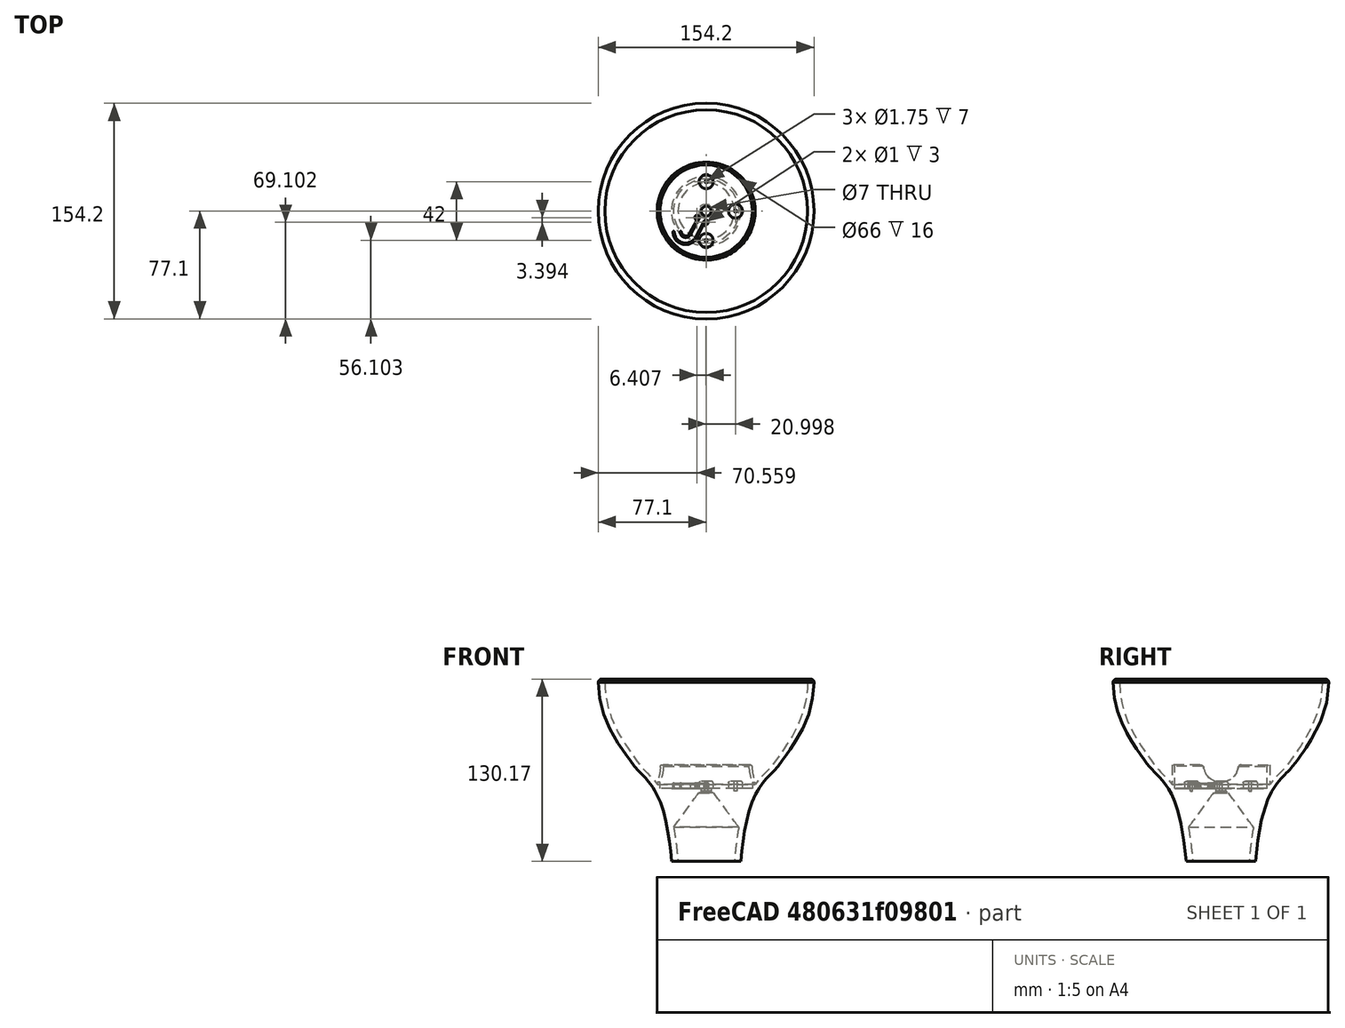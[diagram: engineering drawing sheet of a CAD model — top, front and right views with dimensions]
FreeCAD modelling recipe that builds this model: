
FCSTD DOCUMENT  (FreeCAD 0.21R33771 (Git))
Label: lampshade post-merge
License: All rights reserved
LicenseURL: http://en.wikipedia.org/wiki/All_rights_reserved
objects: Sketcher::SketchObject×10, PartDesign::Pocket×5, PartDesign::Fillet×4, PartDesign::Pad×3, PartDesign::Body×3, PartDesign::Chamfer×2, Part::Feature×2, Mesh::Feature×1, Part::Refine×1, PartDesign::Revolution×1, Part::FeaturePython×1, PartDesign::FeatureBase×1, PartDesign::PolarPattern×1, App::Part×1
note: 49 computed .brp shape members not serialized (recipe doc carries the construction recipe); baked Part::Feature solids carry a one-line shape summary decoded from their .brp

FEATURE [Sketcher::SketchObject] Sketch001
  FullyConstrained = true
  MapMode = 5
  Support = -> [XY_Plane]
  sketch-geometry (1):
    g0: Circle CenterX=0 CenterY=0 CenterZ=0 NormalX=0 NormalY=0 NormalZ=1 AngleXU=0 Radius=35
  constraints (2):
    c: Coincident(g0,g-1)
    c: Diameter(g0) = 70
FEATURE [PartDesign::Pad] Pad
  Direction = (0,0,1)
  Length = 20
  Length2 = 10
  Profile = -> Sketch001
  ReferenceAxis = -> Sketch001 [N_Axis]
  Type = 0
FEATURE [Sketcher::SketchObject] Sketch
  FullyConstrained = true
  MapMode = 5
  Placement = pos=(0,0,20) rot=(0,0,1;0rad)
  Support = -> [Pad]
  sketch-geometry (1):
    g0: Circle CenterX=0 CenterY=0 CenterZ=0 NormalX=0 NormalY=0 NormalZ=1 AngleXU=0 Radius=33
  constraints (2):
    c: Coincident(g0,g-1)
    c: Diameter(g0) = 66
FEATURE [PartDesign::Pocket] Pocket
  BaseFeature = -> Pad
  Direction = (0,0,-1)
  Length = 17
  Length2 = 5
  Profile = -> Sketch
  ReferenceAxis = -> Sketch [N_Axis]
  Type = 0
FEATURE [Sketcher::SketchObject] Sketch002
  FullyConstrained = false
  MapMode = 5
  Placement = pos=(0,0,3) rot=(0,0,1;0rad)
  Support = -> [Pocket]
  sketch-geometry (4):
    g0: Circle CenterX=-0.00194019 CenterY=0.00345167 CenterZ=0 NormalX=0 NormalY=0 NormalZ=1 AngleXU=0 Radius=21
    g1: Circle CenterX=0 CenterY=21.0035 CenterZ=0 NormalX=0 NormalY=0 NormalZ=1 AngleXU=0 Radius=5
    g2: Circle CenterX=20.9981 CenterY=0 CenterZ=0 NormalX=0 NormalY=0 NormalZ=1 AngleXU=0 Radius=5
    g3: Circle CenterX=0 CenterY=-20.9965 CenterZ=0 NormalX=0 NormalY=0 NormalZ=1 AngleXU=0 Radius=5
  constraints (10):
    c: Diameter(g0) = 42
    c: PointOnObject(g1,g0)
    c: PointOnObject(g2,g0)
    c: PointOnObject(g3,g0)
    c: PointOnObject(g3,g-2)
    c: PointOnObject(g2,g-1)
    c: PointOnObject(g1,g-2)
    c: Equal(g1,g2)
    c: Equal(g2,g3)
    c: Diameter(g1) = 10
FEATURE [PartDesign::Pad] Pad001
  BaseFeature = -> Pocket
  Direction = (0,0,1)
  Length = 5
  Length2 = 10
  Profile = -> Sketch002
  ReferenceAxis = -> Sketch002 [N_Axis]
  Type = 0
FEATURE [Sketcher::SketchObject] Sketch003
  ExternalGeometry = -> [Pad001]
  FullyConstrained = true
  MapMode = 5
  Placement = pos=(0,0,8) rot=(0,0,1;0rad)
  Support = -> [Pad001]
  sketch-geometry (3):
    g0: Circle CenterX=0 CenterY=21.0035 CenterZ=0 NormalX=0 NormalY=0 NormalZ=1 AngleXU=0 Radius=0.875
    g1: Circle CenterX=0 CenterY=-20.9965 CenterZ=0 NormalX=0 NormalY=0 NormalZ=1 AngleXU=0 Radius=0.875
    g2: Circle CenterX=20.9981 CenterY=0 CenterZ=0 NormalX=0 NormalY=0 NormalZ=1 AngleXU=0 Radius=0.875
  constraints (6):
    c: Coincident(g0,g-3)
    c: Coincident(g1,g-4)
    c: Coincident(g2,g-5)
    c: Equal(g0,g1)
    c: Equal(g1,g2)
    c: Diameter(g0) = 1.75
FEATURE [PartDesign::Pocket] Pocket001
  BaseFeature = -> Pad001
  Direction = (0,0,-1)
  Length = 7
  Length2 = 5
  Profile = -> Sketch003
  ReferenceAxis = -> Sketch003 [N_Axis]
  Type = 0
FEATURE [Sketcher::SketchObject] Sketch004
  FullyConstrained = true
  MapMode = 5
  Placement = pos=(0,0,3) rot=(0,0,1;0rad)
  Support = -> [Pocket001]
  sketch-geometry (1):
    g0: Circle CenterX=0 CenterY=0 CenterZ=0 NormalX=0 NormalY=0 NormalZ=1 AngleXU=0 Radius=3.5
  constraints (3):
    c: PointOnObject(g0,g-1)
    c: Diameter(g0) = 7
    c: PointOnObject(g0,g-2)
FEATURE [PartDesign::Pocket] Pocket002
  BaseFeature = -> Pocket001
  Direction = (0,0,-1)
  Length = 10
  Length2 = 5
  Profile = -> Sketch004
  ReferenceAxis = -> Sketch004 [N_Axis]
  Type = 0
FEATURE [PartDesign::Chamfer] Chamfer
  Angle = 45
  Base = -> Pocket002 [Edge2,Edge5,Edge4]
  BaseFeature = -> Pocket002
  ChamferType = 0
  FlipDirection = false
  Size = 1
  Size2 = 1
  SupportTransform = false
  UseAllEdges = false
FEATURE [Sketcher::SketchObject] Sketch005
  ExternalGeometry = -> [Chamfer]
  FullyConstrained = false
  MapMode = 5
  Placement = pos=(0,0,3) rot=(0,0,1;0rad)
  Support = -> [Chamfer]
  sketch-geometry (21):
    g0: LineSegment StartX=0 StartY=0 StartZ=0 EndX=-12.3375 EndY=-23.2904 EndZ=0
    g1: LineSegment StartX=-3.33785 StartY=-6.30109 StartZ=0 EndX=-5.10519 EndY=-5.36488 EndZ=0
    g2: LineSegment StartX=-3.33785 StartY=-6.30109 StartZ=0 EndX=-1.5705 EndY=-7.2373 EndZ=0
    g3: ArcOfCircle CenterX=-0.134531 CenterY=-7.99797 CenterZ=0 NormalX=0 NormalY=0 NormalZ=1 AngleXU=0 Radius=1.625 StartAngle=3.81788 EndAngle=8.93763
    g4: ArcOfCircle CenterX=-6.54116 CenterY=-4.60421 CenterZ=0 NormalX=0 NormalY=0 NormalZ=1 AngleXU=0 Radius=1.625 StartAngle=5.79576 EndAngle=10.9054
    g5: ArcOfCircle CenterX=-14.6925 CenterY=-14.9185 CenterZ=0 NormalX=0 NormalY=0 NormalZ=1 AngleXU=0 Radius=4 StartAngle=3.14159 EndAngle=5.83833
    g6: LineSegment StartX=-11.1578 StartY=-16.7909 StartZ=0 EndX=-9.3905 EndY=-17.7271 EndZ=0
    g7: LineSegment StartX=-9.3905 StartY=-17.7271 StartZ=0 EndX=-7.62315 EndY=-18.6633 EndZ=0
    g8: LineSegment StartX=-14.9937 StartY=-18.9071 StartZ=0 EndX=-14.9184 EndY=-17.91 EndZ=0
    g9: ArcOfCircle CenterX=-14.6925 CenterY=-14.9185 CenterZ=0 NormalX=0 NormalY=0 NormalZ=1 AngleXU=0 Radius=3 StartAngle=3.14159 EndAngle=5.79576
    g10: LineSegment StartX=-8.32768 StartY=-19.765 StartZ=0 EndX=-7.53208 EndY=-20.3708 EndZ=0
    g11: LineSegment StartX=-11.0819 StartY=-16.6398 StartZ=0 EndX=-5.10541 EndY=-5.36528 EndZ=0
    g12: LineSegment StartX=-7.62315 StartY=-18.6633 StartZ=0 EndX=-1.5705 EndY=-7.2373 EndZ=0
    g13: LineSegment StartX=-6.48386 StartY=-18.6087 StartZ=0 EndX=-1.40187 EndY=-9.01506 EndZ=0
    g14: LineSegment StartX=-12.0419 StartY=-16.3235 StartZ=0 EndX=-6.68757 EndY=-6.2226 EndZ=0
    g15: LineSegment StartX=-14.6925 StartY=-14.9185 StartZ=0 EndX=-23.6925 EndY=-14.9185 EndZ=0
    g16: ArcOfCircle CenterX=-23.1925 CenterY=-14.9185 CenterZ=0 NormalX=0 NormalY=0 NormalZ=1 AngleXU=0 Radius=0.5 StartAngle=0 EndAngle=3.14159
    g17: ArcOfCircle CenterX=-18.1925 CenterY=-14.9185 CenterZ=0 NormalX=0 NormalY=0 NormalZ=1 AngleXU=0 Radius=0.5 StartAngle=-9e-16 EndAngle=3.14159
    g18: GeomPoint X=-22.6925 Y=-14.9185 Z=0
    g19: ArcOfCircle CenterX=-14.6925 CenterY=-14.9185 CenterZ=0 NormalX=0 NormalY=0 NormalZ=1 AngleXU=0 Radius=9 StartAngle=3.14159 EndAngle=5.86071
    g20: ArcOfCircle CenterX=-14.6925 CenterY=-14.9185 CenterZ=0 NormalX=0 NormalY=0 NormalZ=1 AngleXU=0 Radius=8 StartAngle=3.14159 EndAngle=5.79604
  constraints (45):
    c: Coincident(g0,g-3)
    c: Coincident(g2,g1)
    c: PointOnObject(g1,g0)
    c: Perpendicular(g0,g1)
    c: Perpendicular(g0,g2)
    c: Equal(g1,g2)
    c: Distance(g1,g2) = 4
    c: PointOnObject(g1,g4)
    c: Perpendicular(g4,g1)
    c: Equal(g4,g3)
    c: Diameter(g3) = 3.25
    c: Diameter(g5) = 8
    c: PointOnObject(g6,g5)
    c: Coincident(g7,g6)
    c: Perpendicular(g5,g6)
    c: Equal(g6,g7)
    c: PointOnObject(g6,g0)
    c: Perpendicular(g0,g6)
    c: PointOnObject(g8,g5)
    c: Perpendicular(g5,g8)
    c: Distance(g8) = 1  'cable guide wall thickness'
    c: Coincident(g9,g5)
    c: PointOnObject(g8,g9)
    c: Equal(g8,g10)
    c: Tangent(g12,g3) = 1.5708
    c: Parallel(g14,g11)
    c: Parallel(g12,g13)
    c: Coincident(g15,g5)
    c: Horizontal(g15)
    c: PointOnObject(g16,g15)
    c: PointOnObject(g17,g15)
    c: PointOnObject(g18,g16)
    c: Coincident(g19,g13)
    c: Coincident(g20,g12) = -1.5708
    c: Perpendicular(g3,g2) = 1.5708
    c: Coincident(g3,g13)
    c: Coincident(g4,g14)
    c: Tangent(g4,g11) = -1.5708
    c: Tangent(g16,g19) = -1.5708
    c: Tangent(g16,g20) = 1.5708
    c: Tangent(g17,g9) = 1.5708
    c: Tangent(g5,g17) = -1.5708
    c: Tangent(g9,g14) = -1.5708
    c: PointOnObject(g9,g15)
    c: Coincident(g5,g11)
FEATURE [PartDesign::Pad] Pad002
  BaseFeature = -> Chamfer
  Direction = (0,0,1)
  Length = 3.75
  Length2 = 10
  Profile = -> Sketch005
  ReferenceAxis = -> Sketch005 [N_Axis]
  Type = 0
FEATURE [Sketcher::SketchObject] Sketch006
  ExternalGeometry = -> [Pad002]
  FullyConstrained = true
  MapMode = 5
  Placement = pos=(0,0,6.75) rot=(0,0,1;0rad)
  Support = -> [Pad002]
  sketch-geometry (2):
    g0: Circle CenterX=-6.54116 CenterY=-4.60421 CenterZ=0 NormalX=0 NormalY=0 NormalZ=1 AngleXU=0 Radius=0.5
    g1: Circle CenterX=-0.134531 CenterY=-7.99797 CenterZ=0 NormalX=0 NormalY=0 NormalZ=1 AngleXU=0 Radius=0.5
  constraints (4):
    c: Coincident(g0,g-3)
    c: Coincident(g1,g-4)
    c: Equal(g0,g1)
    c: Diameter(g0) = 1
FEATURE [PartDesign::Pocket] Pocket003
  BaseFeature = -> Pad002
  Direction = (0,0,-1)
  Length = 3
  Length2 = 5
  Profile = -> Sketch006
  ReferenceAxis = -> Sketch006 [N_Axis]
  Type = 0
FEATURE [PartDesign::Fillet] Fillet
  Base = -> Pocket003 [Edge15]
  BaseFeature = -> Pocket003
  Radius = 1
  SupportTransform = false
  UseAllEdges = false
FEATURE [PartDesign::Fillet] Fillet001
  Base = -> Fillet [Edge21]
  BaseFeature = -> Fillet
  Radius = 1
  SupportTransform = false
  UseAllEdges = false
FEATURE [PartDesign::Fillet] Fillet002
  Base = -> Fillet001 [Edge13]
  BaseFeature = -> Fillet001
  Radius = 1
  SupportTransform = false
  UseAllEdges = false
FEATURE [PartDesign::Fillet] Fillet003
  Base = -> Fillet002 [Edge49,Edge47,Edge51]
  BaseFeature = -> Fillet002
  Radius = 1
  SupportTransform = false
  UseAllEdges = false
FEATURE [Mesh::Feature] Head_v1
FEATURE [Part::Feature] Head_v002
  shape: large baked B-rep (101 MB .brp); summary skipped
FEATURE [Part::Refine] Head_v003
  Source = -> Head_v002
FEATURE [Part::Feature] Head_v003_cs
  shape: bbox 3e-07 x 154.9 x 129.2 mm, 0 faces, 0 solids (baked)
FEATURE [Sketcher::SketchObject] Sketch007
  FullyConstrained = false
  Placement = pos=(0,0,0) rot=(0,1,0;1.5708rad)
  sketch-geometry (18):
    g0: GeomPoint X=-127.837 Y=-77.1037 Z=0
    g1: BSplineCurve PolesCount=7 KnotsCount=5 Degree=3 IsPeriodic=0
    g2-g8: Circle x7 (B-spline internal-alignment scaffolding for g1; pole/knot coordinates omitted)
    g9-g13: GeomPoint x5 (B-spline internal-alignment scaffolding for g1; pole/knot coordinates omitted)
    g14: LineSegment StartX=-127.837 StartY=-77.1037 StartZ=0 EndX=-127.837 EndY=-72.4339 EndZ=0
    g15: BSplineCurve PolesCount=7 KnotsCount=5 Degree=3 IsPeriodic=0
    g16: LineSegment StartX=0 StartY=-24.806 StartZ=0 EndX=0 EndY=-20.1362 EndZ=0
    g17: ArcOfCircle CenterX=-127.837 CenterY=-74.7688 CenterZ=0 NormalX=0 NormalY=0 NormalZ=1 AngleXU=0 Radius=2.33488 StartAngle=1.5708 EndAngle=4.71239
  constraints (26):
    c: Block(g1)
    c: InternalAlignment(g2,g1)
    c: Weight(g2) = 1
    c: InternalAlignment(g3,g1)
    c: Equal(g3,g2)
    c: InternalAlignment(g4,g1)
    c: Equal(g4,g2)
    c: InternalAlignment(g5,g1)
    c: Equal(g5,g2)
    c: InternalAlignment(g6,g1)
    c: Equal(g6,g2)
    c: InternalAlignment(g7,g1)
    c: Equal(g7,g2)
    c: InternalAlignment(g8,g1)
    c: Equal(g8,g2)
    c: InternalAlignment(g9-g13 -> g1) x5
    c: Coincident(g14,g1)
    c: Vertical(g14)
    c: Block(g15)
    c: Coincident(g16,g1)
    c: Coincident(g16,g15)
    c: Vertical(g16)
    c: PointOnObject(g15,g17)
    c: PointOnObject(g17,g14)
    c: Coincident(g17,g14)
    c: Coincident(g17,g1)
FEATURE [PartDesign::Revolution] Revolution
  Angle = 360
  Axis = (2e-16,0,-1)
  Base = (0,0,0)
  Placement = pos=(0,0,0) rot=(0,1,0;1.5708rad)
  Profile = -> Sketch007
  ReferenceAxis = -> Sketch007 [H_Axis]
  Reversed = true
FEATURE [PartDesign::Body] Body001  label="Lampshade"
  Group = -> [Sketch007,Revolution]
  Origin = -> Origin002
  Tip = -> Revolution
FEATURE [Sketcher::SketchObject] Sketch008
  FullyConstrained = true
  MapMode = 5
  Placement = pos=(0,0,20) rot=(0,0,1;0rad)
  Support = -> [Fillet003]
FEATURE [PartDesign::Body] Body  label="Webcam Mount"
  Group = -> [Sketch,Sketch001,Pad,Pocket,Sketch002,Pad001,Sketch003,Pocket001,Sketch004,Pocket002,Chamfer,Sketch005,Pad002,Sketch006,Pocket003,Fillet,Fillet001,Fillet002,Fillet003,Sketch008]
  Origin = -> Origin
  Placement = pos=(0,0,49) rot=(0,0,1;0rad)
  Tip = -> Fillet003
FEATURE [Part::FeaturePython] Connect  # WARN: FeaturePython — macro-defined, semantics opaque (R4)
  Objects = -> [Body001,Body]
  Tolerance = 0
FEATURE [PartDesign::FeatureBase] BaseFeature
  BaseFeature = -> Connect
FEATURE [PartDesign::Chamfer] Chamfer001
  Angle = 45
  Base = -> BaseFeature [Edge110]
  BaseFeature = -> BaseFeature
  ChamferType = 0
  FlipDirection = false
  Size = 26
  Size2 = 1
  SupportTransform = false
  UseAllEdges = false
FEATURE [Sketcher::SketchObject] Sketch009
  ExternalGeometry = -> [Chamfer001]
  FullyConstrained = true
  MapMode = 4
  Placement = pos=(33,0,0) rot=(0.58,0.58,0.58;2.0944rad)
  sketch-geometry (6):
    g0: ArcOfCircle CenterX=-14.7902 CenterY=66.5 CenterZ=0 NormalX=0 NormalY=0 NormalZ=1 AngleXU=0 Radius=2.5 StartAngle=0.167448 EndAngle=1.5708
    g1: ArcOfCircle CenterX=14.7902 CenterY=66.5 CenterZ=0 NormalX=0 NormalY=0 NormalZ=1 AngleXU=0 Radius=2.5 StartAngle=1.5708 EndAngle=2.97414
    g2: GeomPoint X=-14.7902 Y=69 Z=0
    g3: GeomPoint X=14.7902 Y=69 Z=0
    g4: LineSegment StartX=-14.7902 StartY=69 StartZ=0 EndX=14.7902 EndY=69 EndZ=0
    g5: ArcOfCircle CenterX=0 CenterY=69 CenterZ=0 NormalX=0 NormalY=0 NormalZ=1 AngleXU=0 Radius=12.5 StartAngle=3.30904 EndAngle=6.11574
  constraints (16):
    c: Tangent(g0,g-3)
    c: Diameter(g0) = 5
    c: Equal(g0,g1)
    c: PointOnObject(g2,g-3)
    c: PointOnObject(g3,g-3)
    c: PointOnObject(g3,g1)
    c: Coincident(g4,g2)
    c: PointOnObject(g4,g1)
    c: Horizontal(g4)
    c: Coincident(g0,g4)
    c: Tangent(g1,g-3) = -1.5708
    c: PointOnObject(g5,g-2)
    c: PointOnObject(g5,g4)
    c: Diameter(g5) = 25
    c: Tangent(g5,g0) = 1.5708
    c: Tangent(g5,g1) = 1.5708
FEATURE [PartDesign::Pocket] Pocket004
  BaseFeature = -> Chamfer001
  Direction = (-1,1e-16,-2e-16)
  Length = 6
  Length2 = 5
  Midplane = true
  Profile = -> Sketch009
  ReferenceAxis = -> Sketch009 [N_Axis]
  Type = 0
FEATURE [PartDesign::PolarPattern] PolarPattern
  Angle = 360
  Axis = -> Z_Axis003
  BaseFeature = -> Pocket004
  Occurrences = 2
  Originals = -> [Pocket004]
FEATURE [PartDesign::Body] Body002  label="Body"
  BaseFeature = -> Connect
  Group = -> [BaseFeature,Chamfer001,Sketch009,Pocket004,PolarPattern]
  Origin = -> Origin003
  Tip = -> PolarPattern
FEATURE [App::Part] Part
  Group = -> [Body,Body001,Connect,Body002]
  Origin = -> Origin001
